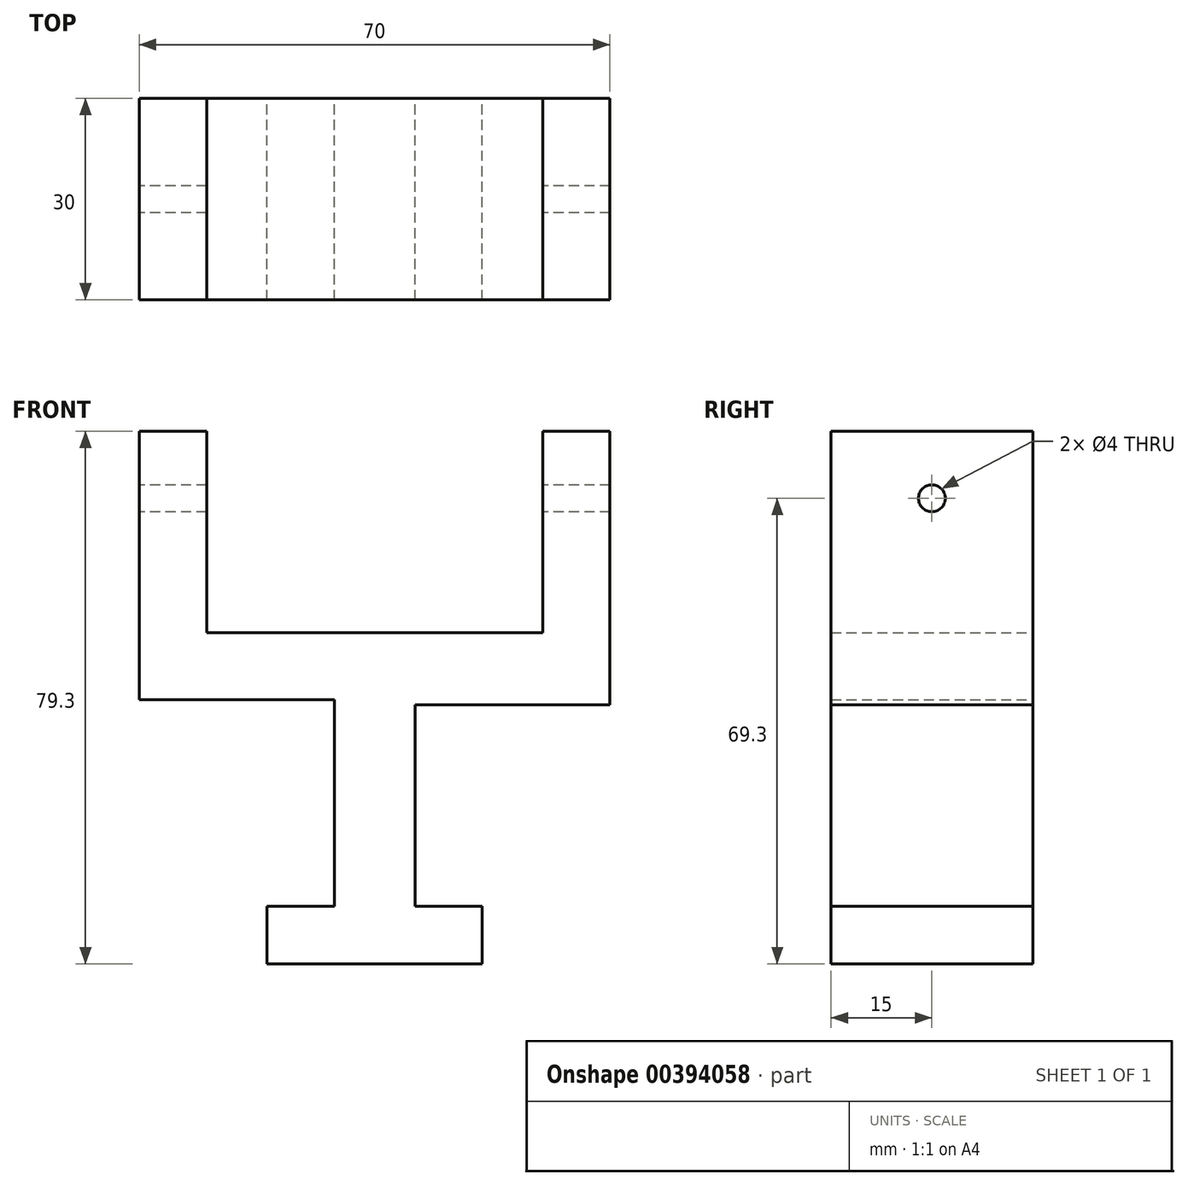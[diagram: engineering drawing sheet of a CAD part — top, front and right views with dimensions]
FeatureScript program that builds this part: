
annotation { "Feature Type Name" : "Feature", "Feature Type Description" : "" }
export const myFeature = defineFeature(function(context is Context, id is Id, definition is map)
    precondition{}
    {
        {
            var Q0;
            Q0=qCreatedBy(makeId("Front.planeOp"),FACE);
            var sketch = newSketch(context, id + "F0", { "sketchPlane" : qUnion([Q0])});
            skLineSegment(sketch, "E0.top", {"start": v(16, -4.3) * mm, "end": v(-16, -4.3) * mm});
            skLineSegment(sketch, "E0.left", {"start": v(16, 4.3) * mm, "end": v(16, -4.3) * mm});
            skLineSegment(sketch, "E0.right", {"start": v(-16, 4.3) * mm, "end": v(-16, -4.3) * mm});
            skPoint(sketch, "E0.middle", {"position": v(0, 0) * mm});
            skLineSegment(sketch, "E1.left", {"start": v(-6, 4.3) * mm, "end": v(-6, 4.3) * mm});
            skLineSegment(sketch, "E1.right", {"start": v(6, 4.3) * mm, "end": v(6, 4.3) * mm});
            skLineSegment(sketch, "E2.left", {"start": v(-6, 4.3) * mm, "end": v(-6, 35) * mm});
            skLineSegment(sketch, "E2.right", {"start": v(6, 4.3) * mm, "end": v(6, 34.3) * mm});
            skLineSegment(sketch, "E3", {"start": v(-35, 35) * mm, "end": v(-35, 75) * mm});
            skLineSegment(sketch, "E4", {"start": v(35, 34.3) * mm, "end": v(35, 75) * mm});
            skLineSegment(sketch, "E5", {"start": v(-35, 75) * mm, "end": v(-25, 75) * mm});
            skLineSegment(sketch, "E6", {"start": v(35, 75) * mm, "end": v(25, 75) * mm});
            skLineSegment(sketch, "E7", {"start": v(25, 45) * mm, "end": v(25, 75) * mm});
            skLineSegment(sketch, "E8", {"start": v(-35, 35) * mm, "end": v(-6, 35) * mm});
            skLineSegment(sketch, "E9", {"start": v(6, 34.3) * mm, "end": v(35, 34.3) * mm});
            skLineSegment(sketch, "E10", {"start": v(-6, 4.3) * mm, "end": v(-16, 4.3) * mm});
            skLineSegment(sketch, "E11", {"start": v(-16, -4.3) * mm, "end": v(16, -4.3) * mm});
            skLineSegment(sketch, "E12", {"start": v(16, 4.3) * mm, "end": v(6, 4.3) * mm});
            skLineSegment(sketch, "E13", {"start": v(35, 45) * mm, "end": v(-35, 45) * mm});
            skLineSegment(sketch, "E14", {"start": v(-25, 75) * mm, "end": v(-25, 45) * mm});
            skSolve(sketch);
        }
        {
            var Q0;
            Q0=makeQuery(id+"F0.imprint","IMPRINT",FACE,{"disambiguationData":[TD([[makeQuery(id+"F0.imprint","IMPRINT",EDGE,{"derivedFrom":sQuery(id+"F0.wireOp",EDGE,"E0.left")}),-1.0]])]});
            extrude(context, id + "F1", {"entities" : qUnion([Q0]), "depth" : 30 * mm});
        }
        {
            var Q0;
            {var subQ0=sQuery(id+"F0.wireOp",EDGE,"E6");Q0=makeQuery(id+"F0.imprint","IMPRINT",FACE,{"disambiguationData":[TD([[makeQuery(id+"F0.imprint","IMPRINT",EDGE,{"derivedFrom":subQ0}),1.0]])]});}
            extrude(context, id + "F2", {"entities" : qUnion([Q0]), "operationType" : NewBodyOperationType.ADD, "depth" : 30 * mm});
        }
        {
            var Q0;
            {var subQ0=sQuery(id+"F0.wireOp",EDGE,"E5");Q0=makeQuery(id+"F0.imprint","IMPRINT",FACE,{"disambiguationData":[TD([[makeQuery(id+"F0.imprint","IMPRINT",EDGE,{"derivedFrom":subQ0}),-1.0]])]});}
            extrude(context, id + "F3", {"entities" : qUnion([Q0]), "operationType" : NewBodyOperationType.ADD, "depth" : 30 * mm});
        }
        {
            var Q0;
            {var subQ0=sQuery(id+"F0.wireOp",EDGE,"E3");Q0=makeQuery(id+"F3.boolean.opBoolean","MERGE",FACE,{"derivedFrom":[makeQuery(id+"F1.opExtrude","SWEPT_FACE",FACE,{"disambiguationData":[OSD([subQ0])]}),makeQuery(id+"F3.opExtrude","SWEPT_FACE",FACE,{"disambiguationData":[OSD([subQ0])]})]});}
            var sketch = newSketch(context, id + "F4", { "sketchPlane" : qUnion([Q0])});
            skCircle(sketch, "E15", {"center": v(15, 65) * mm, "radius": 2 * mm});
            skPoint(sketch, "E15.centerSnap0", {"position": v(15, 75) * mm});
            skSolve(sketch);
        }
        {
            var Q0;
            Q0 = qSketchRegion(id + "F4", true);
            extrude(context, id + "F5", {"entities" : qUnion([Q0]), "operationType" : NewBodyOperationType.REMOVE, "endBound" : BoundingType.THROUGH_ALL, "oppositeDirection" : true, "depth" : 25 * mm});
        }
    });
